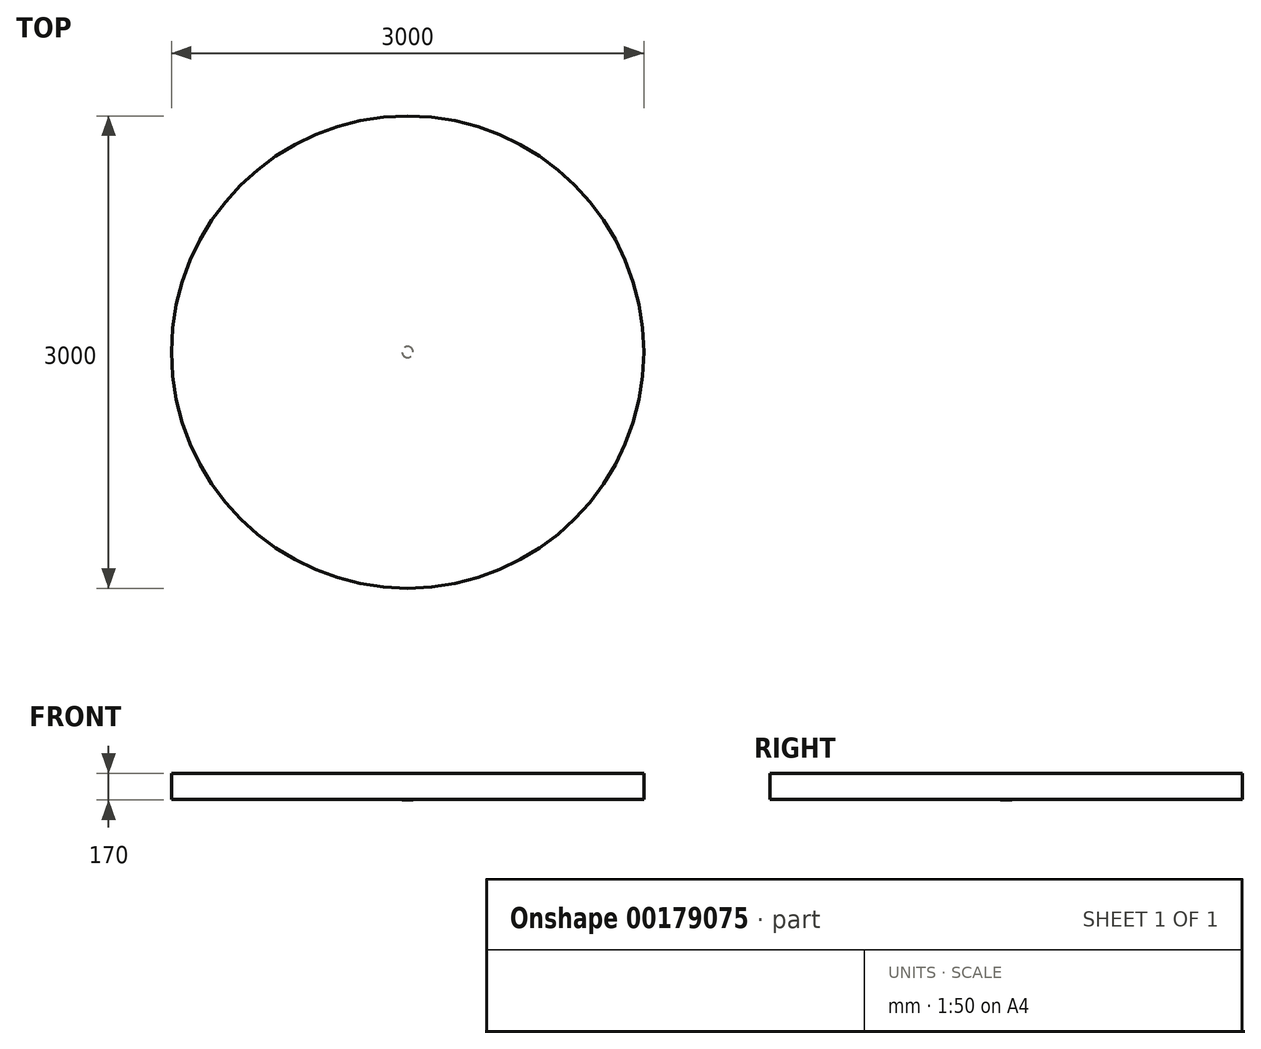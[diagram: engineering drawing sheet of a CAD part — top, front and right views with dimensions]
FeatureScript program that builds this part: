
annotation { "Feature Type Name" : "Feature", "Feature Type Description" : "" }
export const myFeature = defineFeature(function(context is Context, id is Id, definition is map)
    precondition{}
    {
        {
            var Q0;
            Q0=qCreatedBy(makeId("Top.planeOp"),FACE);
            var sketch = newSketch(context, id + "F0", { "sketchPlane" : qUnion([Q0])});
            skCircle(sketch, "E0", {"center": v(0, 0) * mm, "radius": 35.41 * mm});
            skSolve(sketch);
        }
        {
            var Q0;
            Q0=makeQuery(id+"F0.imprint","IMPRINT",FACE,{"disambiguationData":[TD([[makeQuery(id+"F0.imprint","IMPRINT",EDGE,{"derivedFrom":sQuery(id+"F0.wireOp",EDGE,"E0")}),1.0]])]});
            extrude(context, id + "F1", {"entities" : qUnion([Q0]), "depth" : 5 * mm});
        }
        {
            var Q0;
            Q0=makeQuery(id+"F1.opExtrude","CAP_FACE",FACE,{"disambiguationData":[OSD([sQuery(id+"F0.wireOp",EDGE,"E0")])],"isStart":false});
            var sketch = newSketch(context, id + "F2", { "sketchPlane" : qUnion([Q0])});
            skPoint(sketch, "E1.middle", {"position": v(0, 0) * mm});
            skCircle(sketch, "E2", {"center": v(0, 0) * mm, "radius": 1500 * mm});
            skSolve(sketch);
        }
        {
            var Q0;
            Q0=makeQuery(id+"F2.imprint","IMPRINT",FACE,{"disambiguationData":[TD([[makeQuery(id+"F2.imprint","IMPRINT",EDGE,{"derivedFrom":makeQuery(id+"F1.opExtrude","CAP_EDGE",EDGE,{"disambiguationData":[OSD([sQuery(id+"F0.wireOp",EDGE,"E0")])],"isStart":false})}),1.0]])]});
            var Q1;
            Q1=makeQuery(id+"F2.imprint","IMPRINT",FACE,{"disambiguationData":[TD([[makeQuery(id+"F2.imprint","IMPRINT",EDGE,{"derivedFrom":sQuery(id+"F2.wireOp",EDGE,"E2")}),1.0]])]});
            extrude(context, id + "F3", {"entities" : qUnion([Q0, Q1]), "operationType" : NewBodyOperationType.ADD, "depth" : 165 * mm});
        }
    });
